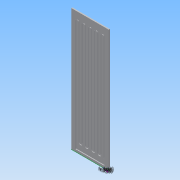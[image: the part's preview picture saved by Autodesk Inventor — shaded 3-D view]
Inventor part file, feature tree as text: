
AUTODESK INVENTOR PART (.ipt)
format: ipt  version: 2013 (Build 170138000, 138)  size: 209,408 bytes
history: native  units: in
note: dims shown in document units (in); Inventor stores cm internally (conversion verified against a paired STEP export)
features: other x7, extrude x2, sketch x2
ambient origin geometry x8: Origin, YZ Plane, XZ Plane, XY Plane, X Axis, Y Axis, Z Axis, Center Point
bodies: Solid1 (feature_tree)
feature tree (11):
  other  "Blocks"
  extrude  "Extrusion1"  Depth=78.0in
  extrude  "Extrusion3"  Depth=66.0in
  sketch  "Sketch5"  dims[d3=0.0in d4=66.0in d6=1.0in d7=2.9in d9=0.24in d10=0.24in d18=1.5in d19=78.0in d20=78.0in d21=22.3125in d22=66.0in d23=2.0in d25=0.24in d26=0.24in d29=2.0in d31=1.5in d32=3.3in d33=1.74in d34=1.0in d35=0.1875in d37=5.46in d38=6.54in d41=66.0in d42=2.0in d43=0.24in d44=0.24in d45=2.0in d46=66.0in d47=2.0in d48=0.48in d49=66.0in d50=2.0in d51=1.0in d52=0.24in d53=0.24in d54=66.0in d55=0.48in d63=0.5in d64=0.0in d73=0.55in d74=0.47in d75=0.5in d76=0.58in d79=1.5in d80=0.48in d81=0.5in d82=0.25in d83=0.5118in d84=0.375in d85=0.2in d86=0.6056in d87=1.1056in]
  sketch  "Sketch1"  dims[d1=23.8125in d2=78.0in]
  other  "LEDPocket"
  other  "TwoLineColumn"
  other  "TwoLineColumnEnd"
  other  "15mm Neon profile"
  other  "15mm Neon profile:1"
  other  "15mm Neon profile:2"
